FCSTD DOCUMENT  (FreeCAD 0.18R16079 (Git))
Label: arc_xml_construction_sample
License: All rights reserved
LicenseURL: http://en.wikipedia.org/wiki/All_rights_reserved
objects: Part::Part2DObjectPython×2, Sketcher::SketchObject×1
note: 3 computed .brp shape members not serialized (recipe doc carries the construction recipe); baked Part::Feature solids carry a one-line shape summary decoded from their .brp

FEATURE [Part::Part2DObjectPython] Sugar_Grove_Road_Horiz  label="Sugar Grove Road Horiz"  # Draft 2D object (typed FeaturePython)
  ChamferSize = 0
  Closed = false
  Datum = (0,0,0)
  End = (0,0,0)
  FilletRadius = 0
  Intersection_Equation = (0,0,0)
  Length = 0
  MakeFace = true
  Method = 0
  Seg_Value = 1
  Start = (0,0,0)
  Subdivisions = 0
  Units = English
FEATURE [Part::Part2DObjectPython] Penrose_Road_West_Horiz  label="Penrose Road West Horiz"  # Draft 2D object (typed FeaturePython)
  ChamferSize = 0
  Closed = false
  Datum = (0,0,0)
  End = (0,0,0)
  FilletRadius = 0
  Intersection_Equation = (0,0,0)
  Length = 0
  MakeFace = true
  Method = 0
  Seg_Value = 1
  Start = (0,0,0)
  Subdivisions = 0
  Units = English
FEATURE [Sketcher::SketchObject] Sketch
  sketch-geometry (16):
    g0: ArcOfCircle CenterX=0 CenterY=0 CenterZ=0 NormalX=0 NormalY=0 NormalZ=1 AngleXU=0 Radius=128.208 StartAngle=0.720521 EndAngle=2.31614
    g1: LineSegment StartX=-86.954 StartY=94.2144 StartZ=0 EndX=9.62861 EndY=183.354 EndZ=0
    g2: LineSegment StartX=9.62861 StartY=183.354 StartZ=0 EndX=96.3436 EndY=84.5888 EndZ=0
    g3: LineSegment StartX=-86.954 StartY=94.2144 StartZ=0 EndX=0 EndY=0 EndZ=0
    g4: LineSegment StartX=0 StartY=0 StartZ=0 EndX=96.3098 EndY=84.6272 EndZ=0
    g5: LineSegment [constr] StartX=9.62861 StartY=183.354 StartZ=0 EndX=85.3856 EndY=253.273 EndZ=0
    g6: LineSegment [constr] StartX=-86.954 StartY=94.2144 StartZ=0 EndX=-86.954 EndY=226.043 EndZ=0
    g7: LineSegment [constr] StartX=9.62861 StartY=183.354 StartZ=0 EndX=9.62861 EndY=253.405 EndZ=0
    g8: LineSegment StartX=0 StartY=0 StartZ=0 EndX=-87.2753 EndY=-93.9168 EndZ=0
    g9: LineSegment StartX=0 StartY=0 StartZ=0 EndX=96.632 EndY=-84.2592 EndZ=0
    g10: ArcOfCircle CenterX=-0.0320312 CenterY=0.609959 CenterZ=0 NormalX=0 NormalY=0 NormalZ=1 AngleXU=0 Radius=128.634 StartAngle=3.96704 EndAngle=5.56267
    g11: LineSegment StartX=-87.2753 StartY=-93.9168 StartZ=0 EndX=9.62861 EndY=-183.354 EndZ=0
    g12: LineSegment StartX=96.632 StartY=-84.2592 StartZ=0 EndX=9.62861 EndY=-183.354 EndZ=0
    g13: LineSegment [constr] StartX=-87.2753 StartY=-93.9168 StartZ=0 EndX=-87.2753 EndY=23.2061 EndZ=0
    g14: LineSegment [constr] StartX=9.62861 StartY=-183.354 StartZ=0 EndX=9.62861 EndY=-73.3071 EndZ=0
    g15: LineSegment [constr] StartX=9.74715 StartY=-183.845 StartZ=0 EndX=66.0118 EndY=-235.775 EndZ=0
  constraints (54):
    c: Coincident(g0,g-1)
    c: Tangent(g2,g0) = 1.5708
    c: Coincident(g1,g2)
    c: Angle(g4,g3) = 1.59522
    c: Coincident(g5,g1)
    c: Parallel(g5,g1)
    c: Angle(g2,g5) = 1.59562
    c: Tangent(g0,g1) = 1.5708
    c: Coincident(g3,g0)
    c: Angle(g2,g3) = 0.0248227
    c: Angle(g1,g-2) = 0.825452
    c: Angle(g-2,g2) = 0.720521
    c: Angle(g-2,g3) = 0.745344
    c: Angle(g4,g-2) = 0.849876
    c: Block(g3)
    c: Block(g4)
    c: Coincident(g6,g0)
    c: Vertical(g6)
    c: Coincident(g7,g1)
    c: Vertical(g7)
    c: Angle(g1,g6) = 0.825452
    c: Angle(g2,g7) = 2.42107
    c: Equal(g8,g3)
    c: Coincident(g11,g8)
    c: Coincident(g12,g11)
    c: Coincident(g13,g8)
    c: Vertical(g13)
    c: Coincident(g14,g11)
    c: Vertical(g14)
    c: Angle(g11,g13) = 2.31615
    c: Angle(g12,g14) = 0.720516
    c: Angle(g8,g9) = 1.60245
    c: Distance(g12) = 131.869
    c: Distance(g3) = 128.208
    c: Distance(g1) = 131.431
    c: Tangent(g11,g10)
    c: Coincident(g8,g10)
    c: Coincident(g9,g10)
    c: Coincident(g9,g12)
    c: Equal(g9,g3)
    c: Tangent(g10,g12)
    c: Coincident(g9,g0)
    c: Coincident(g8,g0)
    c: Symmetric(g11,g1,g-1)
    c: Distance(g9) = 128.208
    c: Angle(g8,g13) = 0.74876
    c: Angle(g14,g11) = 0.825447
    c: Angle(g3,g6) = 2.39625
    c: Distance(g11) = 131.869
    c: Angle(g12,g11) = 1.54596
    c: Parallel(g15,g11)
    c: Angle(g15,g12) = 1.59563
    c: Angle(g11,g8) = 1.56739
    c: Angle(g9,g12) = 1.56739
